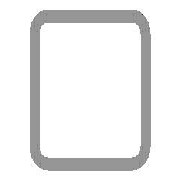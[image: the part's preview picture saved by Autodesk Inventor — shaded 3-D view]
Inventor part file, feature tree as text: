
AUTODESK INVENTOR PART (.ipt)
format: ipt  version: 2025 (Build 290162010, 162A)  size: 153,600 bytes
history: native  units: mm (DEFAULTED — no unit token found)
features: other x3, sketch x2, projected_geometry x2, extrude x1, plane x1
ambient origin geometry x8: Origin, YZ Plane, XZ Plane, XY Plane, X Axis, Y Axis, Z Axis, Center Point
bodies: Solid1 (feature_tree), Body (feature_tree)
feature tree (9):
  other  "Driven Length"
  other  "Start plane"
  other  "End plane"
  extrude  "Extrusion2"  TaperAngle=0.0deg  [1 undecoded]
  sketch  "Sketch3"  dims[d3=5000.0mm d4=0.0mm]
  plane  "Work Plane3"
  sketch  "Sketch5"  dims[d7=8.0mm d9=120.0mm d11=120.0mm d12=4.0mm d13=-0.0mm d14=5000.0mm d15=60.0mm d16=60.0mm d17=90.0deg d18=5000.0mm d19=15.0deg d20=0.0mm d21=0.0mm]
  projected_geometry  "Projected Loop1"
  projected_geometry  "Projected Loop2"
note: 1 required parameter value undecoded (feature->parameter linkage not recoverable at this tier; creation-order binding heuristic only, values carry confidence <= 0.55)
